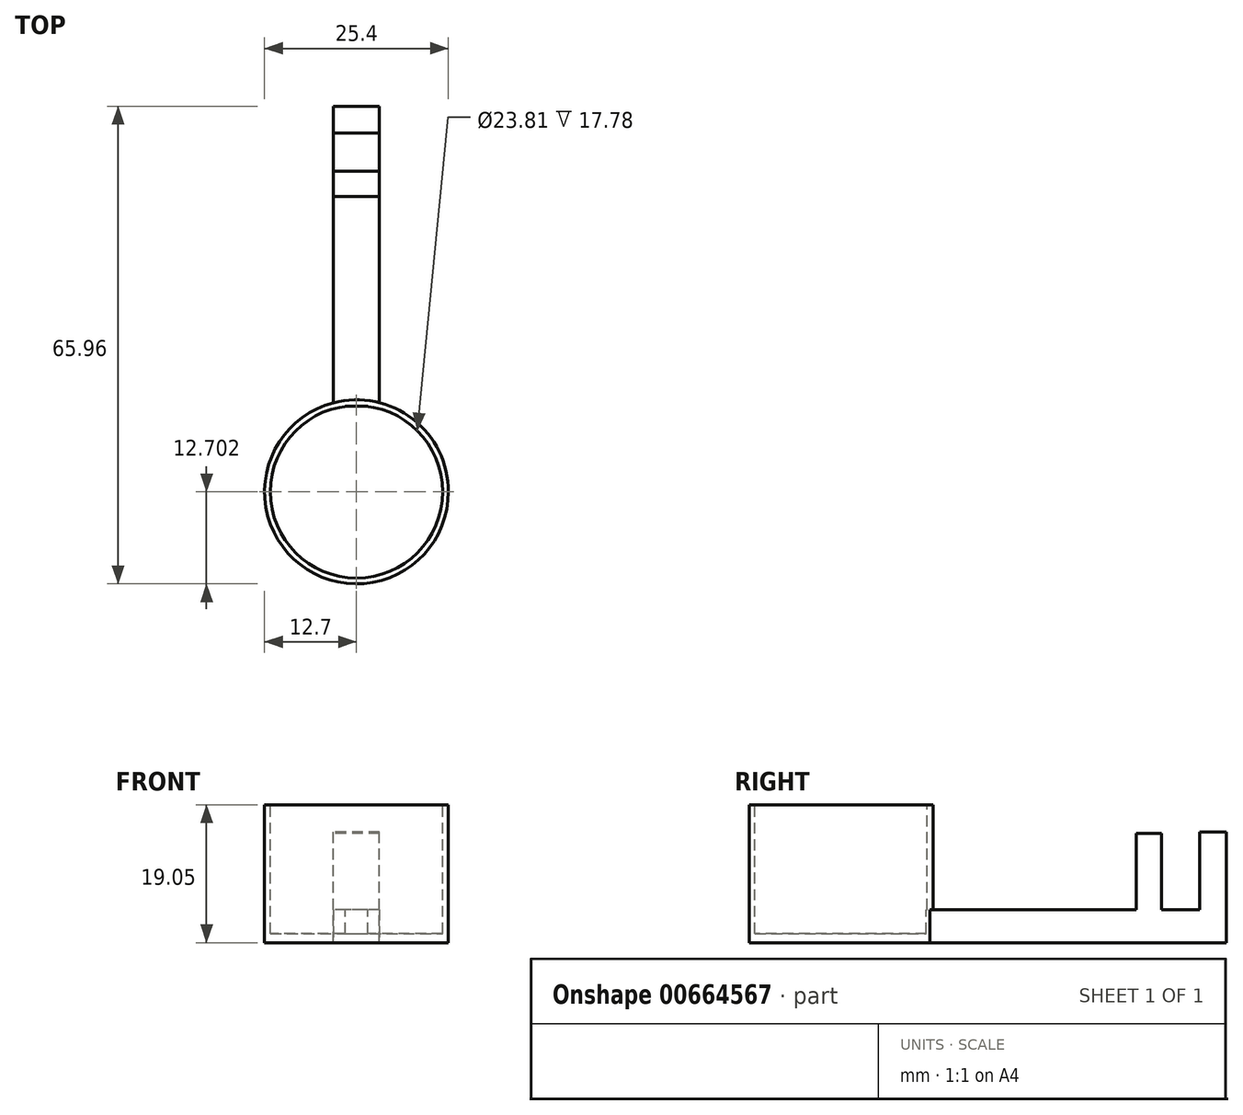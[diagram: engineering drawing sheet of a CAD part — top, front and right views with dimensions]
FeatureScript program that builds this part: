
annotation { "Feature Type Name" : "Feature", "Feature Type Description" : "" }
export const myFeature = defineFeature(function(context is Context, id is Id, definition is map)
    precondition{}
    {
        {
            var Q0;
            Q0=qCreatedBy(makeId("Top.planeOp"),FACE);
            var sketch = newSketch(context, id + "F0", { "sketchPlane" : qUnion([Q0])});
            skCircle(sketch, "E0", {"center": v(0, 0.93) * mm, "radius": 12.7 * mm});
            skSolve(sketch);
        }
        {
            var Q0;
            Q0=makeQuery(id+"F0.imprint","IMPRINT",FACE,{"disambiguationData":[TD([[makeQuery(id+"F0.imprint","IMPRINT",EDGE,{"derivedFrom":sQuery(id+"F0.wireOp",EDGE,"E0")}),1.0]])]});
            extrude(context, id + "F1", {"entities" : qUnion([Q0]), "depth" : 19.05 * mm, "offsetDistance" : 25.4 * mm});
        }
        {
            var Q0;
            Q0=makeQuery(id+"F1.opExtrude","CAP_FACE",FACE,{"disambiguationData":[OSD([sQuery(id+"F0.wireOp",EDGE,"E0")])],"isStart":false});
            var sketch = newSketch(context, id + "F2", { "sketchPlane" : qUnion([Q0])});
            skCircle(sketch, "E1", {"center": v(0, 0.93) * mm, "radius": 11.9 * mm});
            skSolve(sketch);
        }
        {
            var Q0;
            Q0 = qSketchRegion(id + "F2", true);
            extrude(context, id + "F3", {"entities" : qUnion([Q0]), "operationType" : NewBodyOperationType.REMOVE, "oppositeDirection" : true, "depth" : 17.78 * mm, "offsetDistance" : 25.4 * mm});
        }
        {
            var Q0;
            Q0=qCreatedBy(makeId("Right.planeOp"),FACE);
            var sketch = newSketch(context, id + "F4", { "sketchPlane" : qUnion([Q0])});
            skLineSegment(sketch, "E2.bottom", {"start": v(12.73, 0) * mm, "end": v(54.19, 0) * mm});
            skLineSegment(sketch, "E2.top", {"start": v(12.73, 4.57) * mm, "end": v(41.72, 4.57) * mm});
            skLineSegment(sketch, "E2.left", {"start": v(12.73, 0) * mm, "end": v(12.73, 4.57) * mm});
            skLineSegment(sketch, "E2.right", {"start": v(54.19, 0) * mm, "end": v(54.19, 4.57) * mm});
            skLineSegment(sketch, "E3.top", {"start": v(54.19, 15.28) * mm, "end": v(50.5, 15.28) * mm});
            skLineSegment(sketch, "E3.left", {"start": v(54.19, 4.57) * mm, "end": v(54.19, 15.28) * mm});
            skLineSegment(sketch, "E3.right", {"start": v(50.5, 4.57) * mm, "end": v(50.5, 15.28) * mm});
            skLineSegment(sketch, "E4.top", {"start": v(45.23, 15.1) * mm, "end": v(41.72, 15.1) * mm});
            skLineSegment(sketch, "E4.left", {"start": v(45.23, 4.57) * mm, "end": v(45.23, 15.1) * mm});
            skLineSegment(sketch, "E4.right", {"start": v(41.72, 4.57) * mm, "end": v(41.72, 15.1) * mm});
            skLineSegment(sketch, "E5.trimOffspring", {"start": v(45.23, 4.57) * mm, "end": v(50.5, 4.57) * mm});
            skSolve(sketch);
        }
        {
            var Q0;
            Q0=makeQuery(id+"F4.imprint","IMPRINT",FACE,{"disambiguationData":[TD([[makeQuery(id+"F4.imprint","IMPRINT",EDGE,{"derivedFrom":sQuery(id+"F4.wireOp",EDGE,"E2.bottom")}),1.0]])]});
            extrude(context, id + "F5", {"entities" : qUnion([Q0]), "operationType" : NewBodyOperationType.ADD, "endBound" : BoundingType.SYMMETRIC, "depth" : 6.35 * mm, "offsetDistance" : 25.4 * mm});
        }
    });
